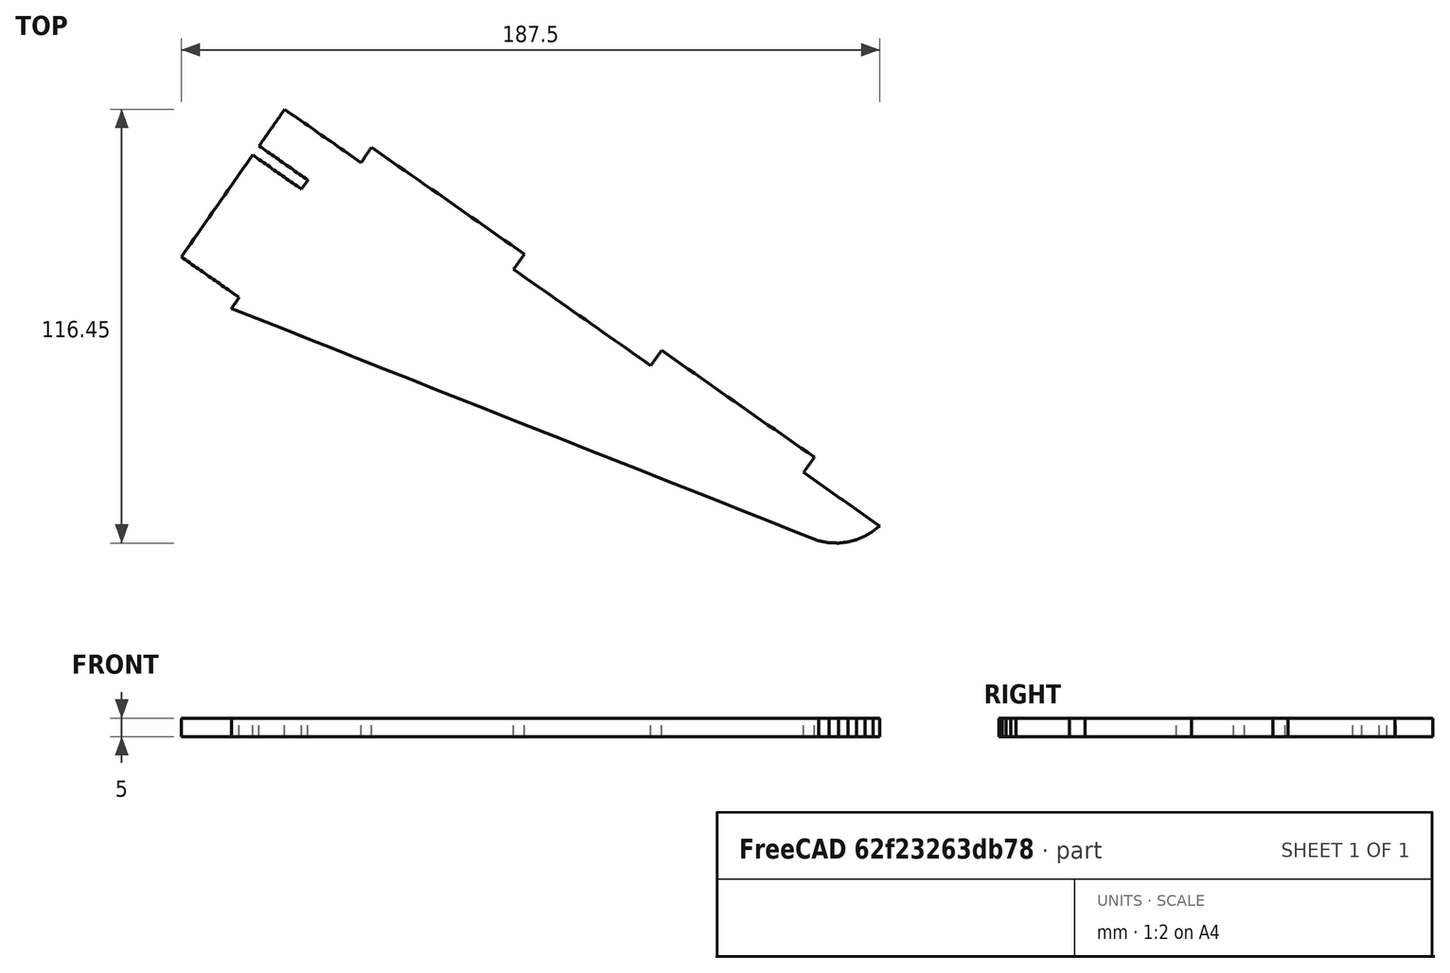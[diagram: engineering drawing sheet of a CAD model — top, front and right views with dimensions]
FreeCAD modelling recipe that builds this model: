
FCSTD DOCUMENT  (FreeCAD 0.19R)
Label: F-35_v2_parts_11
License: All rights reserved
LicenseURL: http://en.wikipedia.org/wiki/All_rights_reserved
objects: App::DocumentObjectGroup×2, PartDesign::CoordinateSystem×2, App::FeaturePython×1, Sketcher::SketchObject×1, PartDesign::Pad×1, PartDesign::Body×1, App::Part×1
note: 6 computed .brp shape members not serialized (recipe doc carries the construction recipe); baked Part::Feature solids carry a one-line shape summary decoded from their .brp

FEATURE [App::DocumentObjectGroup] Parts
FEATURE [PartDesign::CoordinateSystem] LCS_Origin
  AttacherType = Attacher::AttachEngine3D
  MapMode = 2
  Support = -> [X_Axis]
FEATURE [App::DocumentObjectGroup] Constraints
FEATURE [App::FeaturePython] Variables  # WARN: FeaturePython — macro-defined, semantics opaque (R4)
FEATURE [Sketcher::SketchObject] Sketch010
  FullyConstrained = false
  sketch-geometry (25):
    g0: BSplineCurve PolesCount=2 KnotsCount=2 Degree=1 IsPeriodic=0
    g1: BSplineCurve PolesCount=2 KnotsCount=2 Degree=1 IsPeriodic=0
    g2: BSplineCurve PolesCount=2 KnotsCount=2 Degree=1 IsPeriodic=0
    g3: BSplineCurve PolesCount=2 KnotsCount=2 Degree=1 IsPeriodic=0
    g4: BSplineCurve PolesCount=2 KnotsCount=2 Degree=1 IsPeriodic=0
    g5: BSplineCurve PolesCount=2 KnotsCount=2 Degree=1 IsPeriodic=0
    g6: BSplineCurve PolesCount=2 KnotsCount=2 Degree=1 IsPeriodic=0
    g7: BSplineCurve PolesCount=2 KnotsCount=2 Degree=1 IsPeriodic=0
    g8: BSplineCurve PolesCount=2 KnotsCount=2 Degree=1 IsPeriodic=0
    g9: BSplineCurve PolesCount=2 KnotsCount=2 Degree=1 IsPeriodic=0
    g10: BSplineCurve PolesCount=2 KnotsCount=2 Degree=1 IsPeriodic=0
    g11: BSplineCurve PolesCount=2 KnotsCount=2 Degree=1 IsPeriodic=0
    g12: BSplineCurve PolesCount=2 KnotsCount=2 Degree=1 IsPeriodic=0
    g13: BSplineCurve PolesCount=2 KnotsCount=2 Degree=1 IsPeriodic=0
    g14: BSplineCurve PolesCount=2 KnotsCount=2 Degree=1 IsPeriodic=0
    g15: BSplineCurve PolesCount=2 KnotsCount=2 Degree=1 IsPeriodic=0
    g16: BSplineCurve PolesCount=2 KnotsCount=2 Degree=1 IsPeriodic=0
    g17: BSplineCurve PolesCount=2 KnotsCount=2 Degree=1 IsPeriodic=0
    g18: BSplineCurve PolesCount=2 KnotsCount=2 Degree=1 IsPeriodic=0
    g19: BSplineCurve PolesCount=2 KnotsCount=2 Degree=1 IsPeriodic=0
    g20: BSplineCurve PolesCount=2 KnotsCount=2 Degree=1 IsPeriodic=0
    g21: BSplineCurve PolesCount=2 KnotsCount=2 Degree=1 IsPeriodic=0
    g22: BSplineCurve PolesCount=2 KnotsCount=2 Degree=1 IsPeriodic=0
    g23: BSplineCurve PolesCount=2 KnotsCount=2 Degree=1 IsPeriodic=0
    g24: BSplineCurve PolesCount=2 KnotsCount=2 Degree=1 IsPeriodic=0
  constraints (6):
    c: Coincident(g14,g15)
    c: Coincident(g15,g16)
    c: Coincident(g16,g17)
    c: Coincident(g17,g18)
    c: Coincident(g18,g19)
    c: Coincident(g19,g20)
FEATURE [PartDesign::Pad] Pad009
  Direction = (1,1,1)
  Length = 5
  Length2 = 100
  Profile = -> Sketch010
  Type = 0
FEATURE [PartDesign::Body] Body010  label="Part11"
  Group = -> [Sketch010,Pad009]
  Origin = -> Origin011
  Tip = -> Pad009
FEATURE [PartDesign::CoordinateSystem] LCS_1
  AttacherType = Attacher::AttachEngine3D
  AttachmentOffset = pos=(0,0,0) rot=(0,0,1;0.610865rad)
  MapMode = 7
  Placement = pos=(440.667,-278.993,0) rot=(0.300706,0.953717,0;3.14159rad)
  Support = -> [Pad009]
FEATURE [App::Part] Model
  Configuration = 0
  Group = -> [LCS_Origin,Constraints,Variables,Body010,LCS_1]
  Origin = -> Origin
  Type = Assembly4 Model
